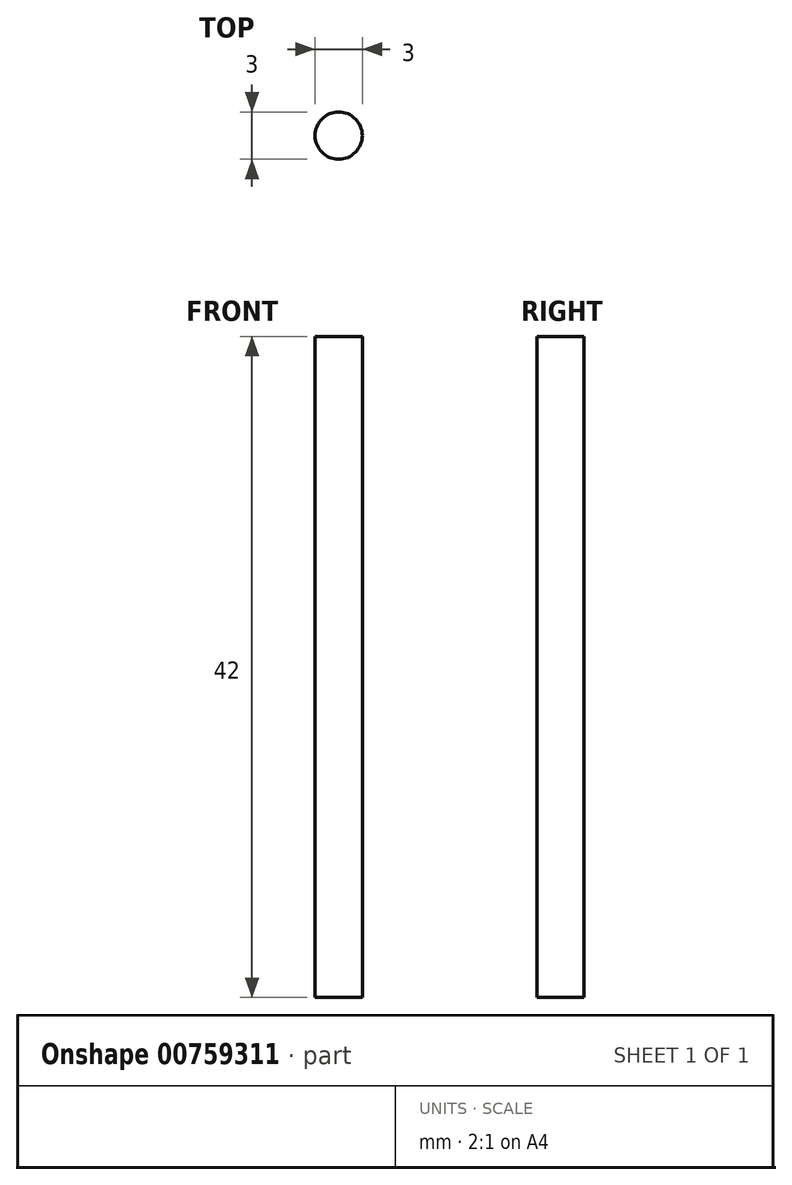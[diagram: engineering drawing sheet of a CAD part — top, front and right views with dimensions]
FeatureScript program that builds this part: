
annotation { "Feature Type Name" : "Feature", "Feature Type Description" : "" }
export const myFeature = defineFeature(function(context is Context, id is Id, definition is map)
    precondition{}
    {
        {
            var Q0;
            Q0=qCreatedBy(makeId("Top.planeOp"),FACE);
            var sketch = newSketch(context, id + "F0", { "sketchPlane" : qUnion([Q0])});
            skCircle(sketch, "E0", {"center": v(0, 0) * mm, "radius": 1.5 * mm});
            skSolve(sketch);
        }
        {
            var Q0;
            Q0 = qSketchRegion(id + "F0", true);
            extrude(context, id + "F1", {"entities" : qUnion([Q0]), "depth" : 42 * mm, "offsetDistance" : 25 * mm});
        }
    });
